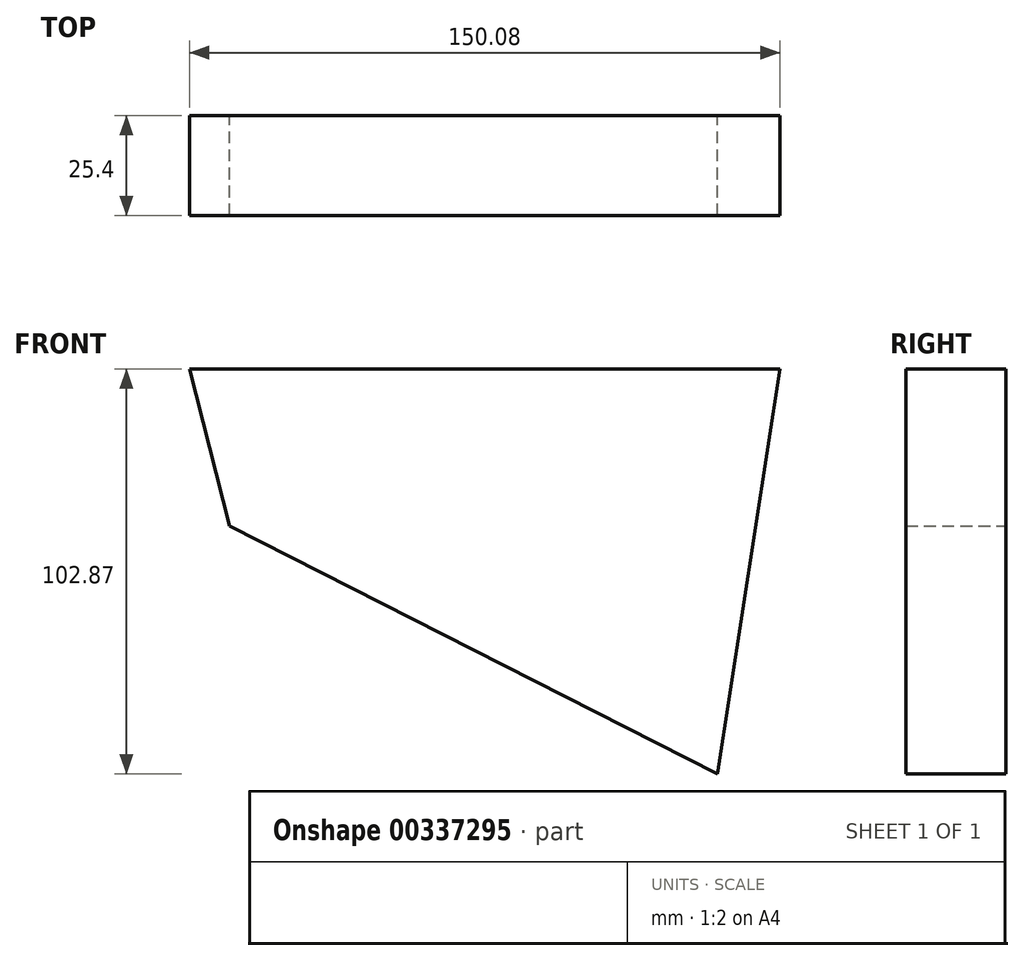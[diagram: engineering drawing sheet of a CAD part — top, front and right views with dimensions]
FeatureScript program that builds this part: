
annotation { "Feature Type Name" : "Feature", "Feature Type Description" : "" }
export const myFeature = defineFeature(function(context is Context, id is Id, definition is map)
    precondition{}
    {
        {
            var Q0;
            Q0=qCreatedBy(makeId("Front.planeOp"),FACE);
            var sketch = newSketch(context, id + "F0", { "sketchPlane" : qUnion([Q0])});
            skLineSegment(sketch, "E0", {"start": v(-87.2, 66.9) * mm, "end": v(62.87, 66.9) * mm});
            skLineSegment(sketch, "E1", {"start": v(62.87, 66.9) * mm, "end": v(47, -35.97) * mm});
            skLineSegment(sketch, "E2", {"start": v(47, -35.97) * mm, "end": v(-77.05, 27.08) * mm});
            skLineSegment(sketch, "E3", {"start": v(-77.05, 27.08) * mm, "end": v(-87.2, 66.9) * mm});
            skSolve(sketch);
        }
        {
            var Q0;
            Q0=makeQuery(id+"F0.imprint","IMPRINT",FACE,{"disambiguationData":[TD([[makeQuery(id+"F0.imprint","IMPRINT",EDGE,{"derivedFrom":sQuery(id+"F0.wireOp",EDGE,"E0")}),-1.0]])]});
            extrude(context, id + "F1", {"entities" : qUnion([Q0]), "depth" : 25.4 * mm});
        }
    });
